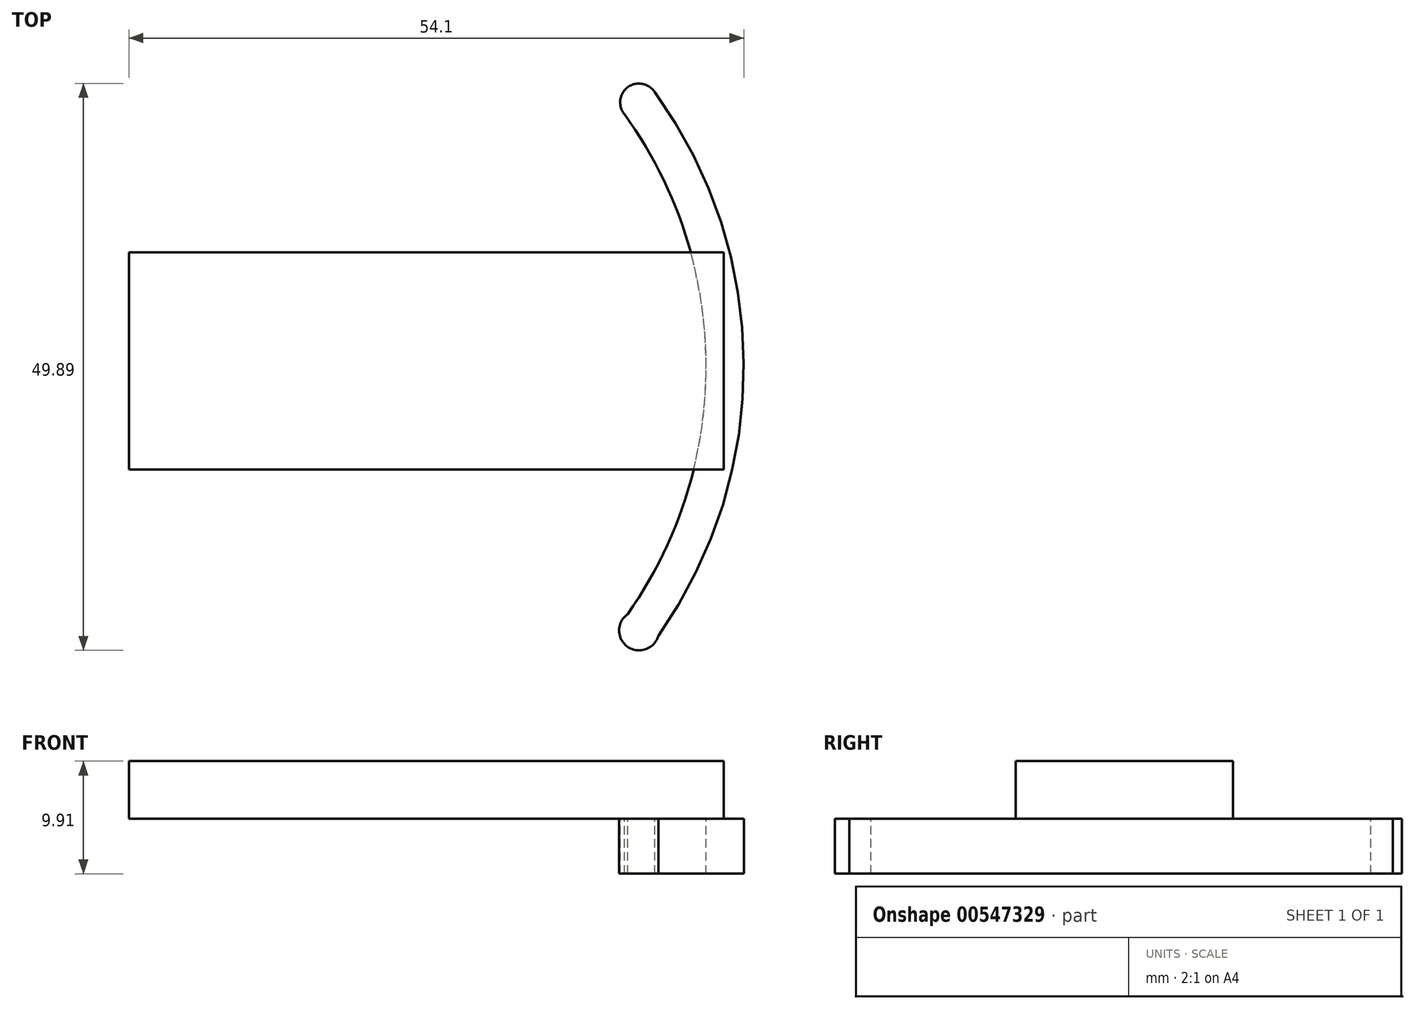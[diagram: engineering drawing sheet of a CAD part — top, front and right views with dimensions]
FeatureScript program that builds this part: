
annotation { "Feature Type Name" : "Feature", "Feature Type Description" : "" }
export const myFeature = defineFeature(function(context is Context, id is Id, definition is map)
    precondition{}
    {
        {
            var Q0;
            Q0=qCreatedBy(makeId("Top.planeOp"),FACE);
            var sketch = newSketch(context, id + "F0", { "sketchPlane" : qUnion([Q0])});
            skArc(sketch, "E0", {"start": v(3, -18.95) * mm, "mid": v(10.53, 5.01) * mm, "end": v(2.7, 28.88) * mm});
            skArc(sketch, "E1.0", {"start": v(0.3, -17.05) * mm, "mid": v(7.23, 5) * mm, "end": v(0.03, 26.94) * mm});
            skArc(sketch, "E2", {"start": v(2.7, 28.88) * mm, "mid": v(0.34, 29.33) * mm, "end": v(0.03, 26.94) * mm});
            skArc(sketch, "E3", {"start": v(0.3, -17.05) * mm, "mid": v(0.3, -19.92) * mm, "end": v(3, -18.95) * mm});
            skSolve(sketch);
        }
        {
            var Q0;
            Q0=makeQuery(id+"F0.imprint","IMPRINT",FACE,{"disambiguationData":[TD([[makeQuery(id+"F0.imprint","IMPRINT",EDGE,{"derivedFrom":sQuery(id+"F0.wireOp",EDGE,"E0")}),1.0]])]});
            extrude(context, id + "F1", {"entities" : qUnion([Q0]), "oppositeDirection" : true, "depth" : 4.83 * mm, "offsetDistance" : 25.4 * mm});
        }
        {
            var Q0;
            Q0=qCreatedBy(makeId("Top.planeOp"),FACE);
            var sketch = newSketch(context, id + "F2", { "sketchPlane" : qUnion([Q0])});
            skLineSegment(sketch, "E4.bottom", {"start": v(8.75, -4.31) * mm, "end": v(-43.57, -4.31) * mm});
            skLineSegment(sketch, "E4.top", {"start": v(8.75, 14.8) * mm, "end": v(-43.57, 14.8) * mm});
            skLineSegment(sketch, "E4.left", {"start": v(8.75, -4.31) * mm, "end": v(8.75, 14.8) * mm});
            skLineSegment(sketch, "E4.right", {"start": v(-43.57, -4.31) * mm, "end": v(-43.57, 14.8) * mm});
            skSolve(sketch);
        }
        {
            var Q0;
            Q0=makeQuery(id+"F2.imprint","IMPRINT",FACE,{"disambiguationData":[TD([[makeQuery(id+"F2.imprint","IMPRINT",EDGE,{"derivedFrom":sQuery(id+"F2.wireOp",EDGE,"E4.bottom")}),-1.0]])]});
            extrude(context, id + "F3", {"entities" : qUnion([Q0]), "operationType" : NewBodyOperationType.ADD, "depth" : 5.08 * mm, "offsetDistance" : 25.4 * mm});
        }
    });
